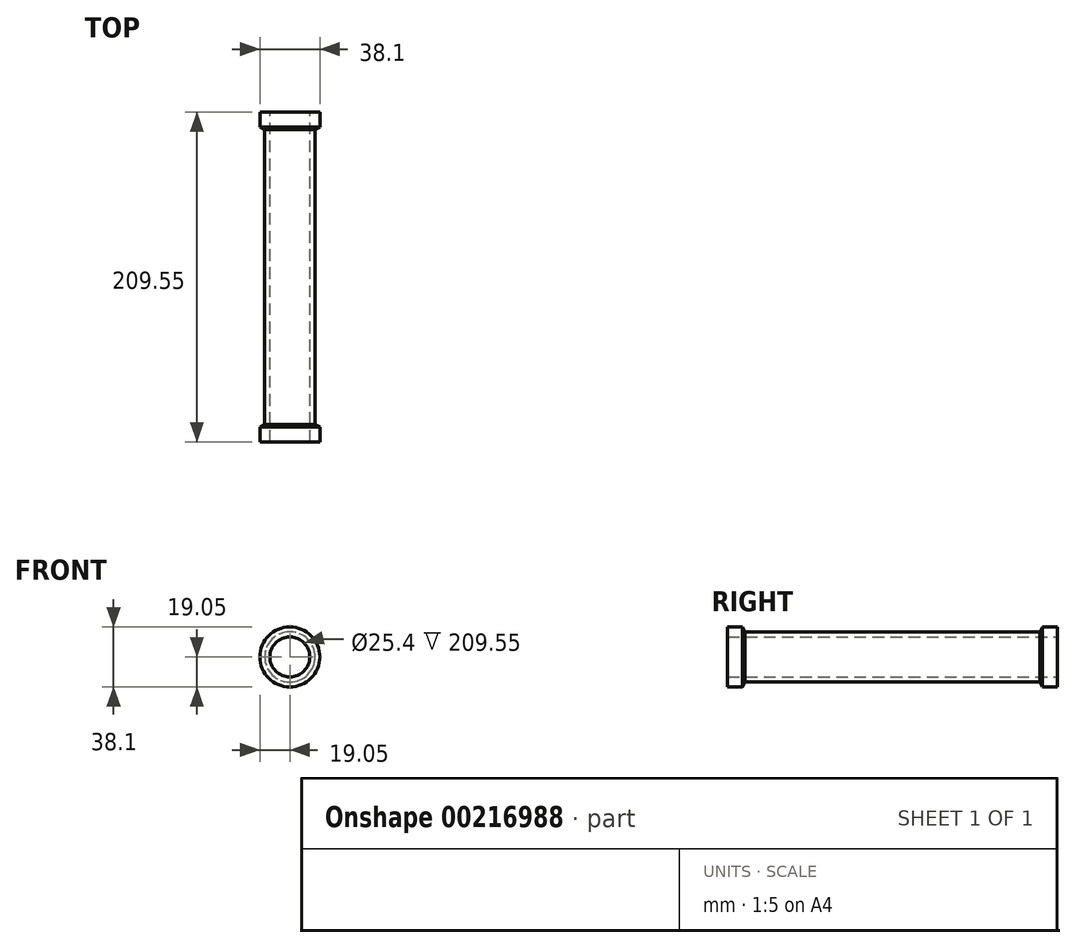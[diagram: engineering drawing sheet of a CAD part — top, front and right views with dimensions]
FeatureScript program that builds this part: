
annotation { "Feature Type Name" : "Feature", "Feature Type Description" : "" }
export const myFeature = defineFeature(function(context is Context, id is Id, definition is map)
    precondition{}
    {
        {
            var Q0;
            Q0=qCreatedBy(makeId("Front.planeOp"),FACE);
            var sketch = newSketch(context, id + "F0", { "sketchPlane" : qUnion([Q0])});
            skCircle(sketch, "E0", {"center": v(0, 0) * mm, "radius": 19.05 * mm});
            skCircle(sketch, "E1", {"center": v(0, 0) * mm, "radius": 12.7 * mm});
            skSolve(sketch);
        }
        {
            var Q0;
            Q0=makeQuery(id+"F0.imprint","IMPRINT",FACE,{"disambiguationData":[TD([[makeQuery(id+"F0.imprint","IMPRINT",EDGE,{"derivedFrom":sQuery(id+"F0.wireOp",EDGE,"E0")}),1.0]])]});
            extrude(context, id + "F1", {"entities" : qUnion([Q0]), "depth" : 152.4 * mm});
        }
        {
            var Q0;
            Q0=makeQuery(id+"F1.opExtrude","CAP_FACE",FACE,{"disambiguationData":[OSD([sQuery(id+"F0.wireOp",EDGE,"E0"),sQuery(id+"F0.wireOp",EDGE,"E1")])],"isStart":false});
            extrude(context, id + "F2", {"entities" : qUnion([Q0]), "operationType" : NewBodyOperationType.ADD, "depth" : 57.15 * mm});
        }
        {
            var Q0;
            Q0=qCreatedBy(makeId("Right.planeOp"),FACE);
            var sketch = newSketch(context, id + "F3", { "sketchPlane" : qUnion([Q0])});
            skLineSegment(sketch, "E2", {"start": v(0, 0) * mm, "end": v(-104.78, 0) * mm, "construction": true});
            skLineSegment(sketch, "E3.bottom", {"start": v(-6.35, -25.66) * mm, "end": v(-203.2, -25.66) * mm});
            skLineSegment(sketch, "E3.top", {"start": v(-6.35, 25.66) * mm, "end": v(-203.2, 25.66) * mm});
            skLineSegment(sketch, "E3.left", {"start": v(-6.35, -25.66) * mm, "end": v(-6.35, 25.66) * mm});
            skLineSegment(sketch, "E3.right", {"start": v(-203.2, -25.66) * mm, "end": v(-203.2, 25.66) * mm});
            skPoint(sketch, "E3.middle", {"position": v(-104.78, 0) * mm});
            skLineSegment(sketch, "E4.bottom", {"start": v(-6.35, -12.45) * mm, "end": v(-203.2, -12.45) * mm});
            skLineSegment(sketch, "E4.top", {"start": v(-6.35, 12.45) * mm, "end": v(-203.2, 12.45) * mm});
            skLineSegment(sketch, "E4.left", {"start": v(-6.35, -12.45) * mm, "end": v(-6.35, 12.45) * mm});
            skLineSegment(sketch, "E4.right", {"start": v(-203.2, -12.45) * mm, "end": v(-203.2, 12.45) * mm});
            skLineSegment(sketch, "E5.bottom", {"start": v(-12.7, -12.45) * mm, "end": v(-196.85, -12.45) * mm});
            skLineSegment(sketch, "E5.top", {"start": v(-12.7, 12.45) * mm, "end": v(-196.85, 12.45) * mm});
            skLineSegment(sketch, "E5.left", {"start": v(-12.7, -12.45) * mm, "end": v(-12.7, 12.45) * mm});
            skLineSegment(sketch, "E5.right", {"start": v(-196.85, -12.45) * mm, "end": v(-196.85, 12.45) * mm});
            skLineSegment(sketch, "E6", {"start": v(-203.2, 25.66) * mm, "end": v(-196.85, 12.45) * mm});
            skLineSegment(sketch, "E7", {"start": v(-196.85, -12.45) * mm, "end": v(-203.2, -25.66) * mm});
            skLineSegment(sketch, "E8", {"start": v(-104.78, 0) * mm, "end": v(-104.78, 10.21) * mm});
            skLineSegment(sketch, "E9.MirrorCS", {"start": v(-6.35, 25.66) * mm, "end": v(-12.7, 12.45) * mm});
            skLineSegment(sketch, "E10", {"start": v(-198.53, 15.94) * mm, "end": v(-11.02, 15.94) * mm});
            skSolve(sketch);
        }
        {
            var Q0;
            {var subQ0=sQuery(id+"F3.wireOp",EDGE,"E3.top");Q0=makeQuery(id+"F3.imprint","IMPRINT",FACE,{"disambiguationData":[TD([[makeQuery(id+"F3.imprint","IMPRINT",EDGE,{"derivedFrom":subQ0}),1.0]])]});}
            var Q1;
            Q1=makeQuery(id+"F2.opExtrude","CAP_EDGE",EDGE,{"disambiguationData":[OSD([sQuery(id+"F0.wireOp",EDGE,"E0")])],"isStart":false});
            revolve(context, id + "F4", {"operationType" : NewBodyOperationType.REMOVE, "entities" : qUnion([Q0]), "axis" : qUnion([Q1]), "revolveType" : RevolveType.FULL, "oppositeDirection" : true});
        }
    });
